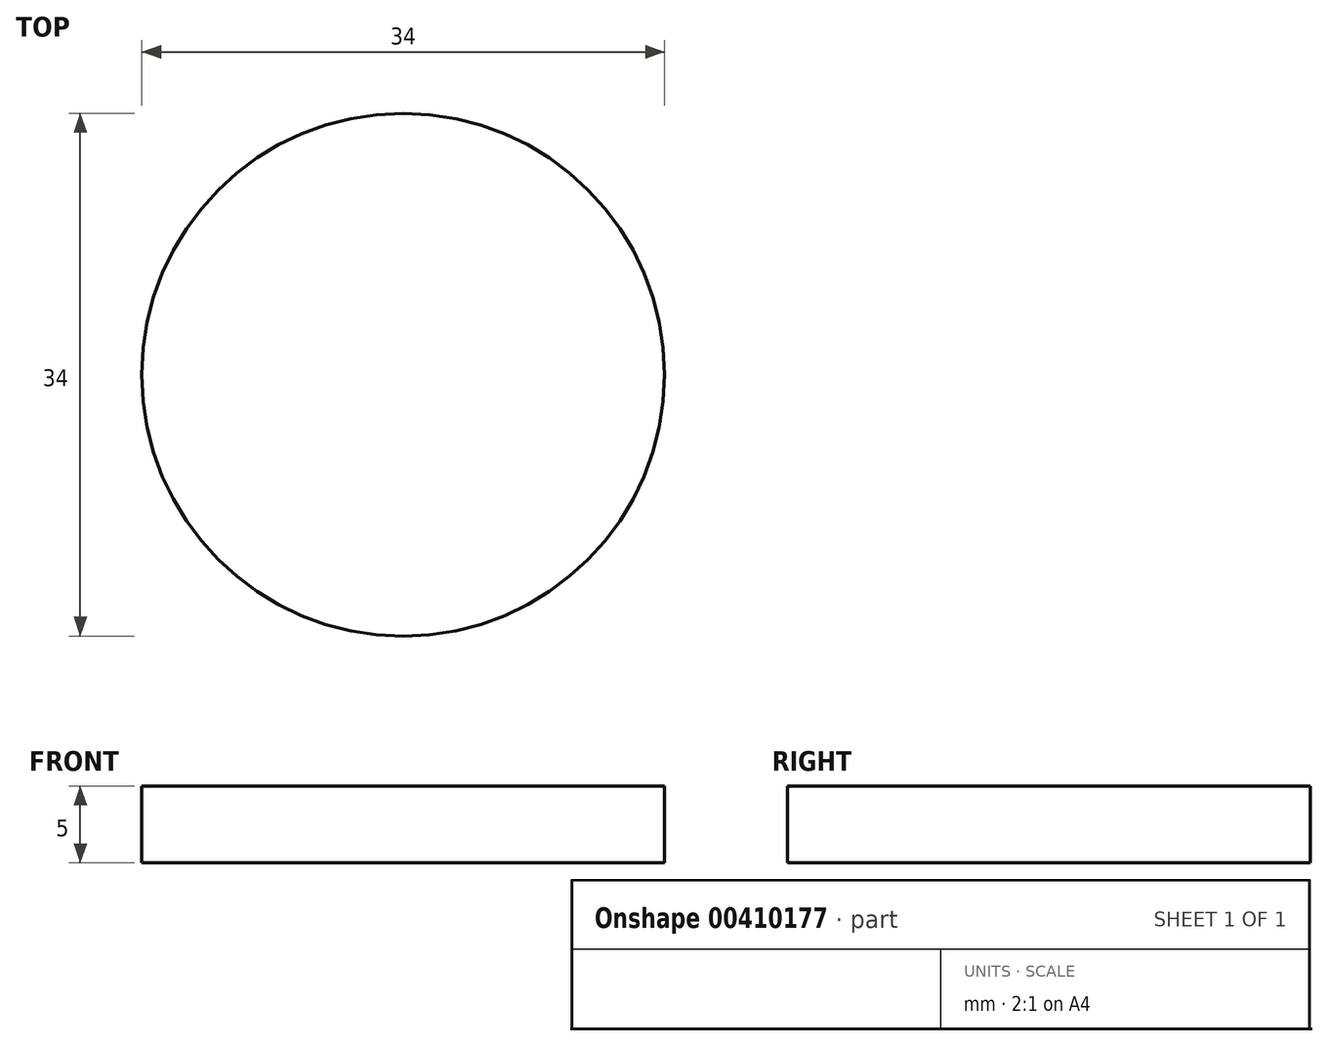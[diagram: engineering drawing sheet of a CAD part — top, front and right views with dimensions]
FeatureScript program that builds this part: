
annotation { "Feature Type Name" : "Feature", "Feature Type Description" : "" }
export const myFeature = defineFeature(function(context is Context, id is Id, definition is map)
    precondition{}
    {
        {
            var Q0;
            Q0=qCreatedBy(makeId("Top.planeOp"),FACE);
            var sketch = newSketch(context, id + "F0", { "sketchPlane" : qUnion([Q0])});
            skCircle(sketch, "E0", {"center": v(0, 0) * mm, "radius": 17 * mm});
            skSolve(sketch);
        }
        {
            var Q0;
            Q0 = qSketchRegion(id + "F0", true);
            extrude(context, id + "F1", {"entities" : qUnion([Q0]), "depth" : 5 * mm});
        }
    });
